# Revit family: ТвінФреш Комфо
name_source: partatom
category: Mechanical Equipment
units: mm (PartAtom-declared; Revit-internal decimal feet)

## family parameters
Always vertical = Yes
Classification = None
Cut with Voids When Loaded = Yes
Part Type = Normal
Room Calculation Point = No
Round Connector Dimension = Use Diameter
Shared = No
Work Plane-Based = No

## types (6) — shared parameters
00_20_Виробник = Вентс
00_20_Назва = Провітрювач
B = 240 mm  [stored 0.787402 ft]
B1 = 186 mm  [stored 0.610236 ft]
D = 157 mm  [stored 0.515092 ft]
Dy = 152 mm  [stored 0.498688 ft]
L = 240 mm  [stored 0.787402 ft]
L2 = 86 mm  [stored 0.282152 ft]
Manufacturer = Вентс
URL = https://vents.ua
b = 180 mm  [stored 0.590551 ft]
b1 = 200 mm  [stored 0.656168 ft]
l1 = 188 mm  [stored 0.616798 ft]
l2 = 126 mm
l3 = 115 mm  [stored 0.377297 ft]
Вага = 5.00 kg
Діаметр = 157 mm  [stored 0.515092 ft]
Клас фільтрації = G3
Класифікація навантаження = HVAC
Кількість фаз = 1
Матеріал зони обслуговуваня = <By Category>
Матеріал корпусу = Пластмаса, непрозора, біла
Напруга = 230 V
Температура повітря, що переміщається = -20...+40 °С
Частота = 50 Hz
zero-valued in all types: Default Elevation

## per-type parameters (varying)
| type | Висота | Довжина | Колпак 2 | Колпак 23 | Максимальний потік повітря | Потужність | Рівень звукового тиску на відстані 3 м | Струм | Ширина |
| ТвінФреш Комфо РA1-50 В.3 | 240 mm  [stored 0.787402 ft] | 385 mm  [stored 1.26312 ft] | No | No | 50.0 m³/h | 7 W | 23 дБА | 0.039 A | 240 mm  [stored 0.787402 ft] |
| ТвінФреш Комфо РA1-50-2 В.3 | 260 mm  [stored 0.853018 ft] | 455 mm | Yes | No | 50.0 m³/h | 7 W | 23 дБА | 0.039 A | 300 mm |
| ТвінФреш Комфо РA1-50-23 В.3 | 260 mm  [stored 0.853018 ft] | 440 mm  [stored 1.44357 ft] | No | Yes | 50.0 m³/h | 7 W | 23 дБА | 0.039 A | 300 mm |
| ТвінФреш Комфо РA1-85 В.3 | 240 mm  [stored 0.787402 ft] | 385 mm  [stored 1.26312 ft] | No | No | 85.0 m³/h | 10 W | 34 дБА | 0.071 A | 240 mm  [stored 0.787402 ft] |
| ТвінФреш Комфо РA1-85-2 В.3 | 260 mm  [stored 0.853018 ft] | 455 mm | Yes | No | 85.0 m³/h | 10 W | 34 дБА | 0.071 A | 300 mm |
| ТвінФреш Комфо РA1-85-23 В.3 | 260 mm  [stored 0.853018 ft] | 440 mm  [stored 1.44357 ft] | No | Yes | 85.0 m³/h | 10 W | 34 дБА | 0.071 A | 300 mm |

note: column(s) folded — value = type name in every type: 00_20_Тип

note: [stored X ft] marks values corroborated as IEEE doubles in the binary element streams (Revit-internal decimal feet)
